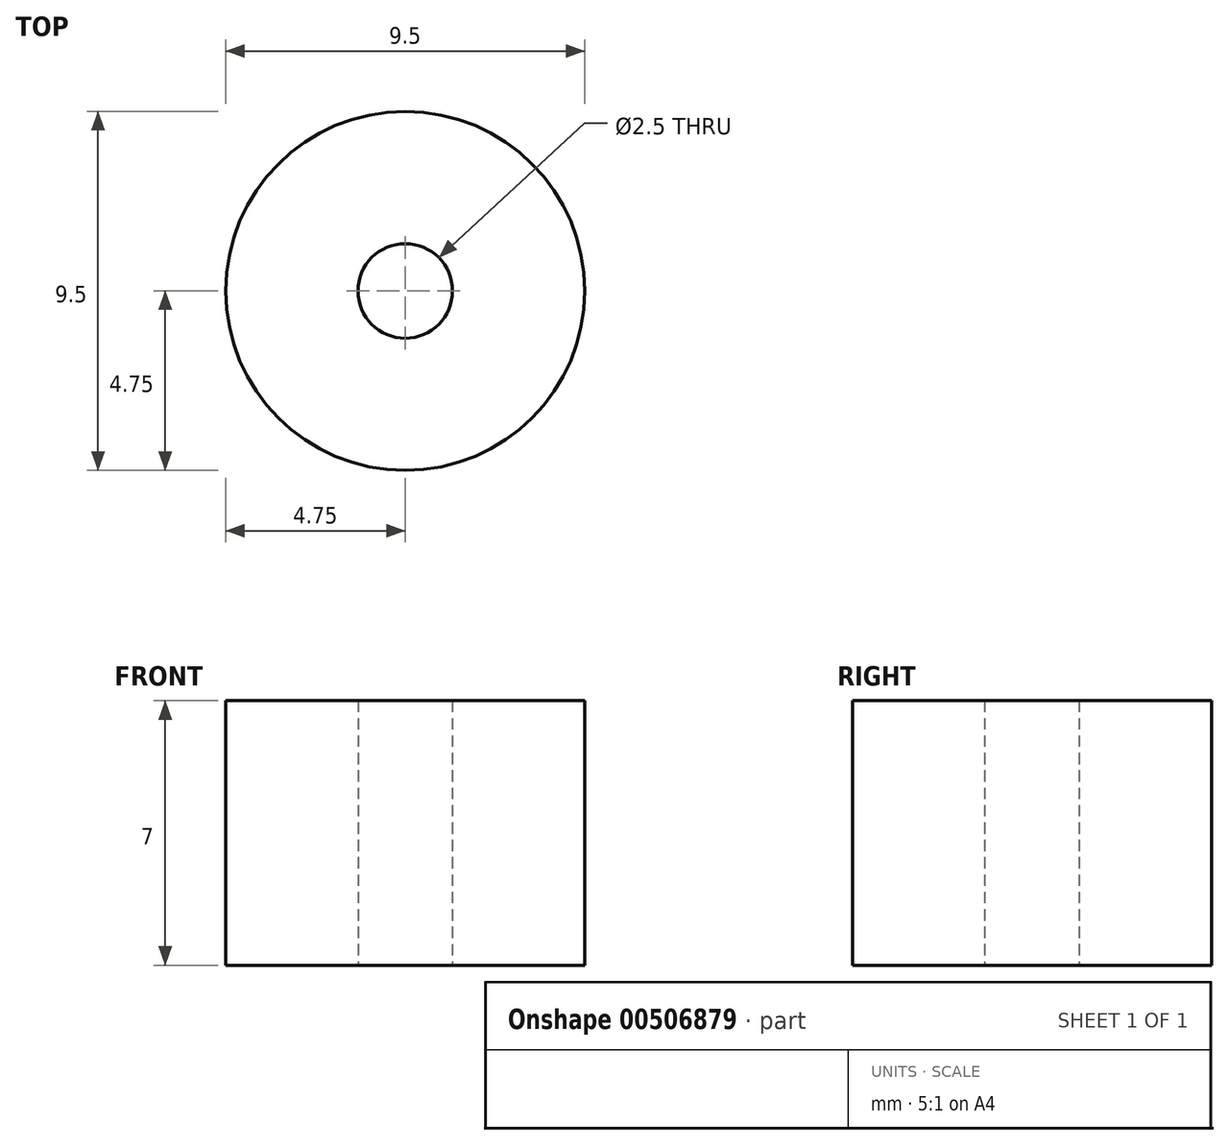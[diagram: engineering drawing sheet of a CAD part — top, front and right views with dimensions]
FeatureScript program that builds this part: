
annotation { "Feature Type Name" : "Feature", "Feature Type Description" : "" }
export const myFeature = defineFeature(function(context is Context, id is Id, definition is map)
    precondition{}
    {
        {
            var Q0;
            Q0=qCreatedBy(makeId("Top.planeOp"),FACE);
            var sketch = newSketch(context, id + "F0", { "sketchPlane" : qUnion([Q0])});
            skCircle(sketch, "E0", {"center": v(0, 0) * mm, "radius": 4.75 * mm});
            skCircle(sketch, "E1", {"center": v(0, 0) * mm, "radius": 1.25 * mm});
            skSolve(sketch);
        }
        {
            var Q0;
            Q0=makeQuery(id+"F0.imprint","IMPRINT",FACE,{"disambiguationData":[TD([[makeQuery(id+"F0.imprint","IMPRINT",EDGE,{"derivedFrom":sQuery(id+"F0.wireOp",EDGE,"E0")}),1.0]])]});
            extrude(context, id + "F1", {"entities" : qUnion([Q0]), "depth" : 7 * mm});
        }
    });
